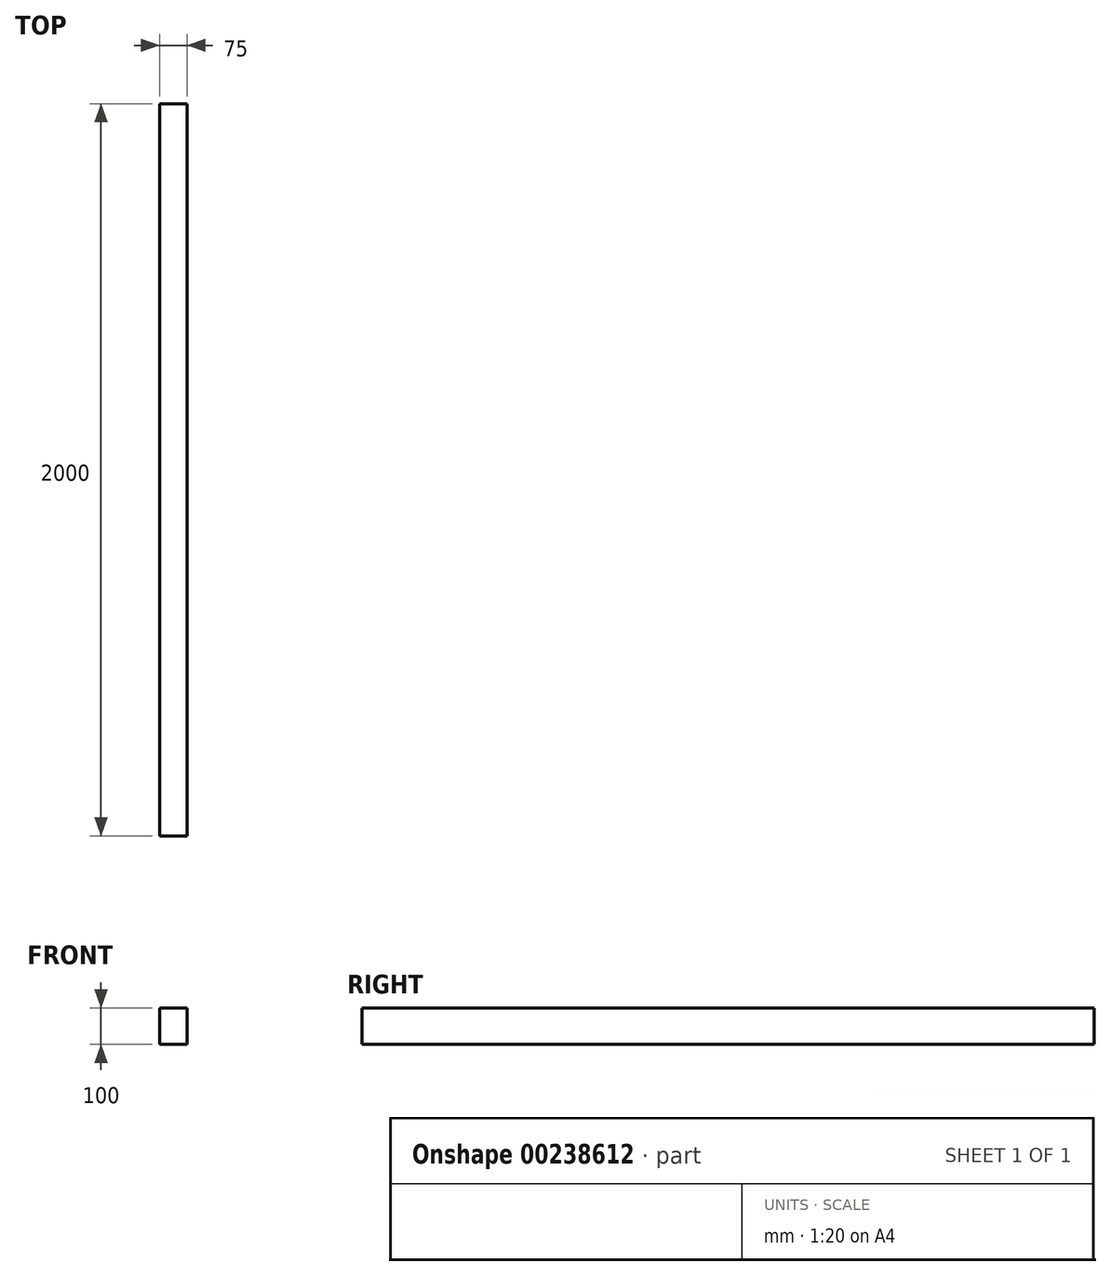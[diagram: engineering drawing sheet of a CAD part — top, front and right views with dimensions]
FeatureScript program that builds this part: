
annotation { "Feature Type Name" : "Feature", "Feature Type Description" : "" }
export const myFeature = defineFeature(function(context is Context, id is Id, definition is map)
    precondition{}
    {
        {
            var Q0;
            Q0=qCreatedBy(makeId("Front.planeOp"),FACE);
            var sketch = newSketch(context, id + "F0", { "sketchPlane" : qUnion([Q0])});
            skLineSegment(sketch, "E0.bottom", {"start": v(37.5, -50) * mm, "end": v(-37.5, -50) * mm});
            skLineSegment(sketch, "E0.top", {"start": v(37.5, 50) * mm, "end": v(-37.5, 50) * mm});
            skLineSegment(sketch, "E0.left", {"start": v(37.5, -50) * mm, "end": v(37.5, 50) * mm});
            skLineSegment(sketch, "E0.right", {"start": v(-37.5, -50) * mm, "end": v(-37.5, 50) * mm});
            skPoint(sketch, "E0.middle", {"position": v(0, 0) * mm});
            skSolve(sketch);
        }
        {
            var Q0;
            Q0=makeQuery(id+"F0.imprint","IMPRINT",FACE,{"disambiguationData":[TD([[makeQuery(id+"F0.imprint","IMPRINT",EDGE,{"derivedFrom":sQuery(id+"F0.wireOp",EDGE,"E0.bottom")}),-1.0]])]});
            extrude(context, id + "F1", {"entities" : qUnion([Q0]), "depth" : 2000 * mm});
        }
    });
